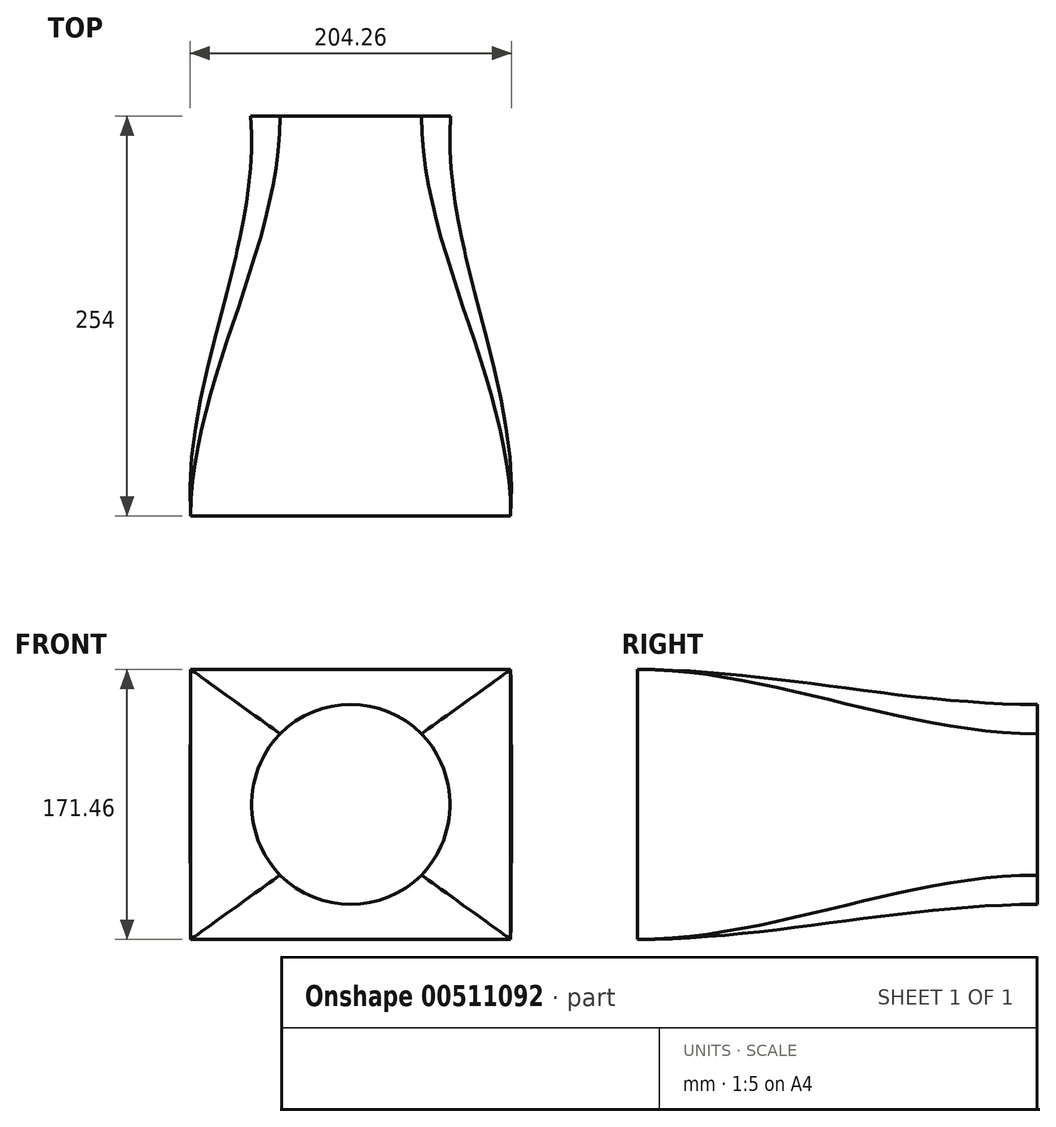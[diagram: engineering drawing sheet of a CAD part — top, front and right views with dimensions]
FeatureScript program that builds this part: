
annotation { "Feature Type Name" : "Feature", "Feature Type Description" : "" }
export const myFeature = defineFeature(function(context is Context, id is Id, definition is map)
    precondition{}
    {
        {
            var Q0;
            Q0=qCreatedBy(makeId("Front.planeOp"),FACE);
            var sketch = newSketch(context, id + "F0", { "sketchPlane" : qUnion([Q0])});
            skLineSegment(sketch, "E0", {"start": v(-44.9, 44.9) * mm, "end": v(44.9, -44.9) * mm, "construction": true});
            skLineSegment(sketch, "E1", {"start": v(44.9, 44.9) * mm, "end": v(-44.9, -44.9) * mm, "construction": true});
            skArc(sketch, "E2", {"start": v(-44.9, 44.9) * mm, "mid": v(-63.5, 0) * mm, "end": v(-44.9, -44.9) * mm});
            skArc(sketch, "E3", {"start": v(44.9, 44.9) * mm, "mid": v(0, 63.5) * mm, "end": v(-44.9, 44.9) * mm});
            skLineSegment(sketch, "E4", {"start": v(44.9, -44.9) * mm, "end": v(44.9, -44.9) * mm});
            skArc(sketch, "E5", {"start": v(-44.9, -44.9) * mm, "mid": v(0, -63.5) * mm, "end": v(44.9, -44.9) * mm});
            skArc(sketch, "E6", {"start": v(44.9, -44.9) * mm, "mid": v(63.5, 0) * mm, "end": v(44.9, 44.9) * mm});
            skSolve(sketch);
        }
        {
            var Q0;
            Q0=qCreatedBy(makeId("Front.planeOp"),FACE);
            cPlane(context, id + "F1", {"entities" : qUnion([Q0]), "cplaneType" : CPlaneType.OFFSET, "offset" : 254 * mm, "width" : 152.4 * mm, "height" : 152.4 * mm});
        }
        {
            var Q0;
            Q0=qCreatedBy(id+"F1.planeOp",FACE);
            var sketch = newSketch(context, id + "F2", { "sketchPlane" : qUnion([Q0])});
            skLineSegment(sketch, "E7.bottom", {"start": v(101.6, 85.73) * mm, "end": v(-101.6, 85.73) * mm});
            skLineSegment(sketch, "E7.top", {"start": v(101.6, -85.73) * mm, "end": v(-101.6, -85.73) * mm});
            skLineSegment(sketch, "E7.left", {"start": v(101.6, 85.73) * mm, "end": v(101.6, -85.73) * mm});
            skLineSegment(sketch, "E7.right", {"start": v(-101.6, 85.73) * mm, "end": v(-101.6, -85.73) * mm});
            skPoint(sketch, "E7.middle", {"position": v(0, 0) * mm});
            skSolve(sketch);
        }
        {
            var Q0;
            Q0=sQuery(id+"F0.wireOp",EDGE,"E3");
            var Q1;
            Q1=sQuery(id+"F2.wireOp",EDGE,"E7.bottom");
            loft(context, id + "F3", {"bodyType" : ToolBodyType.SURFACE, "startCondition" : LoftEndDerivativeType.NORMAL_TO_PROFILE, "startMagnitude" : 1, "endCondition" : LoftEndDerivativeType.NORMAL_TO_PROFILE, "endMagnitude" : 1, "wireProfilesArray" : [{ "wireProfileEntities" : qUnion([Q0]) }, { "wireProfileEntities" : qUnion([Q1]) }]});
        }
        {
            var Q0;
            Q0=sQuery(id+"F0.wireOp",EDGE,"E5");
            var Q1;
            Q1=sQuery(id+"F2.wireOp",EDGE,"E7.top");
            loft(context, id + "F4", {"bodyType" : ToolBodyType.SURFACE, "startCondition" : LoftEndDerivativeType.NORMAL_TO_PROFILE, "startMagnitude" : 1, "endCondition" : LoftEndDerivativeType.NORMAL_TO_PROFILE, "endMagnitude" : 1, "wireProfilesArray" : [{ "wireProfileEntities" : qUnion([Q0]) }, { "wireProfileEntities" : qUnion([Q1]) }]});
        }
        {
            var Q0;
            Q0=sQuery(id+"F0.wireOp",EDGE,"E2");
            var Q1;
            Q1=sQuery(id+"F2.wireOp",EDGE,"E7.right");
            var Q2;
            Q2=makeQuery(id+"F3.opLoft","SWEPT_EDGE",EDGE,{"disambiguationData":[OSD([sQuery(id+"F0.wireOp",VERTEX,"E3.end"),sQuery(id+"F2.wireOp",VERTEX,"E7.bottom.end")])]});
            var Q3;
            Q3=makeQuery(id+"F4.opLoft","SWEPT_EDGE",EDGE,{"disambiguationData":[OSD([sQuery(id+"F0.wireOp",VERTEX,"E5.start"),sQuery(id+"F2.wireOp",VERTEX,"E7.top.end")])]});
            loft(context, id + "F5", {"bodyType" : ToolBodyType.SURFACE, "addGuides" : true, "wireProfilesArray" : [{ "wireProfileEntities" : qUnion([Q0]) }, { "wireProfileEntities" : qUnion([Q1]) }], "guidesArray" : [{ "guideEntities" : qUnion([Q2]), "guideDerivativeType" : LoftGuideDerivativeType.DEFAULT, "guideDerivativeMagnitude" : 1 }, { "guideEntities" : qUnion([Q3]), "guideDerivativeType" : LoftGuideDerivativeType.DEFAULT, "guideDerivativeMagnitude" : 1 }]});
        }
        {
            var Q0;
            Q0=sQuery(id+"F2.wireOp",EDGE,"E7.left");
            var Q1;
            Q1=sQuery(id+"F0.wireOp",EDGE,"E6");
            var Q2;
            Q2=makeQuery(id+"F3.opLoft","SWEPT_EDGE",EDGE,{"disambiguationData":[OSD([sQuery(id+"F0.wireOp",VERTEX,"E3.start"),sQuery(id+"F2.wireOp",VERTEX,"E7.bottom.start")])]});
            var Q3;
            Q3=makeQuery(id+"F4.opLoft","SWEPT_EDGE",EDGE,{"disambiguationData":[OSD([sQuery(id+"F0.wireOp",VERTEX,"E5.end"),sQuery(id+"F2.wireOp",VERTEX,"E7.top.start")])]});
            loft(context, id + "F6", {"bodyType" : ToolBodyType.SURFACE, "addGuides" : true, "wireProfilesArray" : [{ "wireProfileEntities" : qUnion([Q0]) }, { "wireProfileEntities" : qUnion([Q1]) }], "guidesArray" : [{ "guideEntities" : qUnion([Q2]), "guideDerivativeType" : LoftGuideDerivativeType.DEFAULT, "guideDerivativeMagnitude" : 1 }, { "guideEntities" : qUnion([Q3]), "guideDerivativeType" : LoftGuideDerivativeType.DEFAULT, "guideDerivativeMagnitude" : 1 }]});
        }
    });
